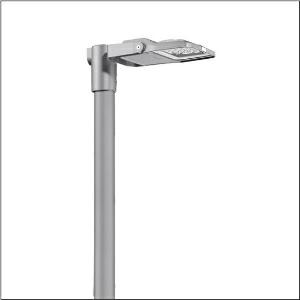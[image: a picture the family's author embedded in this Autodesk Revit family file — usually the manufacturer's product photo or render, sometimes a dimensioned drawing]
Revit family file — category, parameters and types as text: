
# Revit family: floodlight_fl_21_iq_micro___pl33t_5xa7762a2f3a_98d7
name_source: partatom
category: Lighting Fixtures
units: mm (PartAtom-declared; Revit-internal decimal feet)

## family parameters
Cut with Voids When Loaded = No
Host = Face
Light Source = No
Part Type = Normal
Room Calculation Point = No
Round Connector Dimension = Use Diameter
Shared = No

## types (1)
- --- (1 x LED, 2930 lm, 23.1 W, 3000K)
    Apparent Load = 23 VA
    CIE Flux Codes = 26 75 99 100 100
    Color Rendering = 70
    Color Temperature = 3000K
    Default Elevation = 1800 mm
    Description = Floodlight FL 21 iQ micro, floodlight, primary light control with lens, of PMMA, primary optical cover: protective disc, of toughened safety glass, transparent, light distribution: PL33T, light emission: direct distribution, installation type: surface-mounted, LED, High Power LED, rated luminous flux: 2.930lm, luminous efficacy: 127lm/W, light colour: 730, colour temperature: 3000K, control: Auto-Match, Temp-Guard, Night-Set, Smart-Wire, Desk-Remote (wireless, voltage-free reading and setting of iQ features in the workshop via application-optimized NFC function/RFID function), optimised constant luminous flux control (CLO 2.0), Street-Remote, with terminal, 6-pole, mains connection: 220..240V, AC, 50/60Hz, start of lifetime: 23W, end of service life: 24W, reduction: 11W, luminaire housing, of diecast aluminium, powder-coated, Siteco® metallic grey (DB 702S), corrosivity category C5 mid according to DIN EN ISO 12944, sealing non-destructively replaceable, please order mast flange separately, mast bracket, of steel, galvanised, powder-coated, Siteco® metallic grey (DB 702S), protection rating (complete): IP66, insulation class (complete): insulation class II (safety insulation), certification: CE, ENEC, VDE, protection symbol: D, impact resistance: IK07, permissible operating ambient temperature: -40..+40°C, permissible operating ambient temperature for outdoor applications: -40..+50°C, standard: DIN EN 12944, LABS conformity tested according to VDMA 24364:2018-05, packaging unit: 1 piece

Light Distribution: PL33T
    Height = 65 mm
    Lamp = 1 x LED
    Lamp Light Flux = 2930 lm
    Lamp Power = 23.1 W
    Lamp count = 1
    Length = 312 mm
    Luminous efficacy = 127 lm/W
    Manufacturer = Siteco
    ModVariant = No
    Model = 5XA7762A2F3A
    Number of Poles = 1
    OnlyDefault = Yes
    Power Factor = 1
    Product Name = Floodlight FL 21 iQ micro | PL33T
    Product group = floodlight | pylon annexe
    ProductGroupID = 6200
    Protection Class = Protection class II
    Protection Degree = IP 66
    RLX_Detail_Level = 1
    RLX_Emergency_Light_Flux = 0 lm
    RLX_Emergency_Type = 0
    RLX_Emergency_Type_DB = No
    RlxData = <blob elided: 101581 chars, md5=51bd12f2>
    Socket = socket
    Standby Power = 0 W
    System Light Flux = 2930 lm
    System Power = 23 W
    Type Comments = factory setting: luminous flux: 100 % | dim-lin: 254 | 455 mA
    Type Image = l_1007121.jpg
    URL = http://relux.com
    VarID = @adj_118307
    Voltage = 0 V
    Weight = 0.00 kg
    Width = 230 mm

## geometry (parser evidence)
native form markers: Blend x4, Sweep x11
no freeform markers — native parametric forms only
